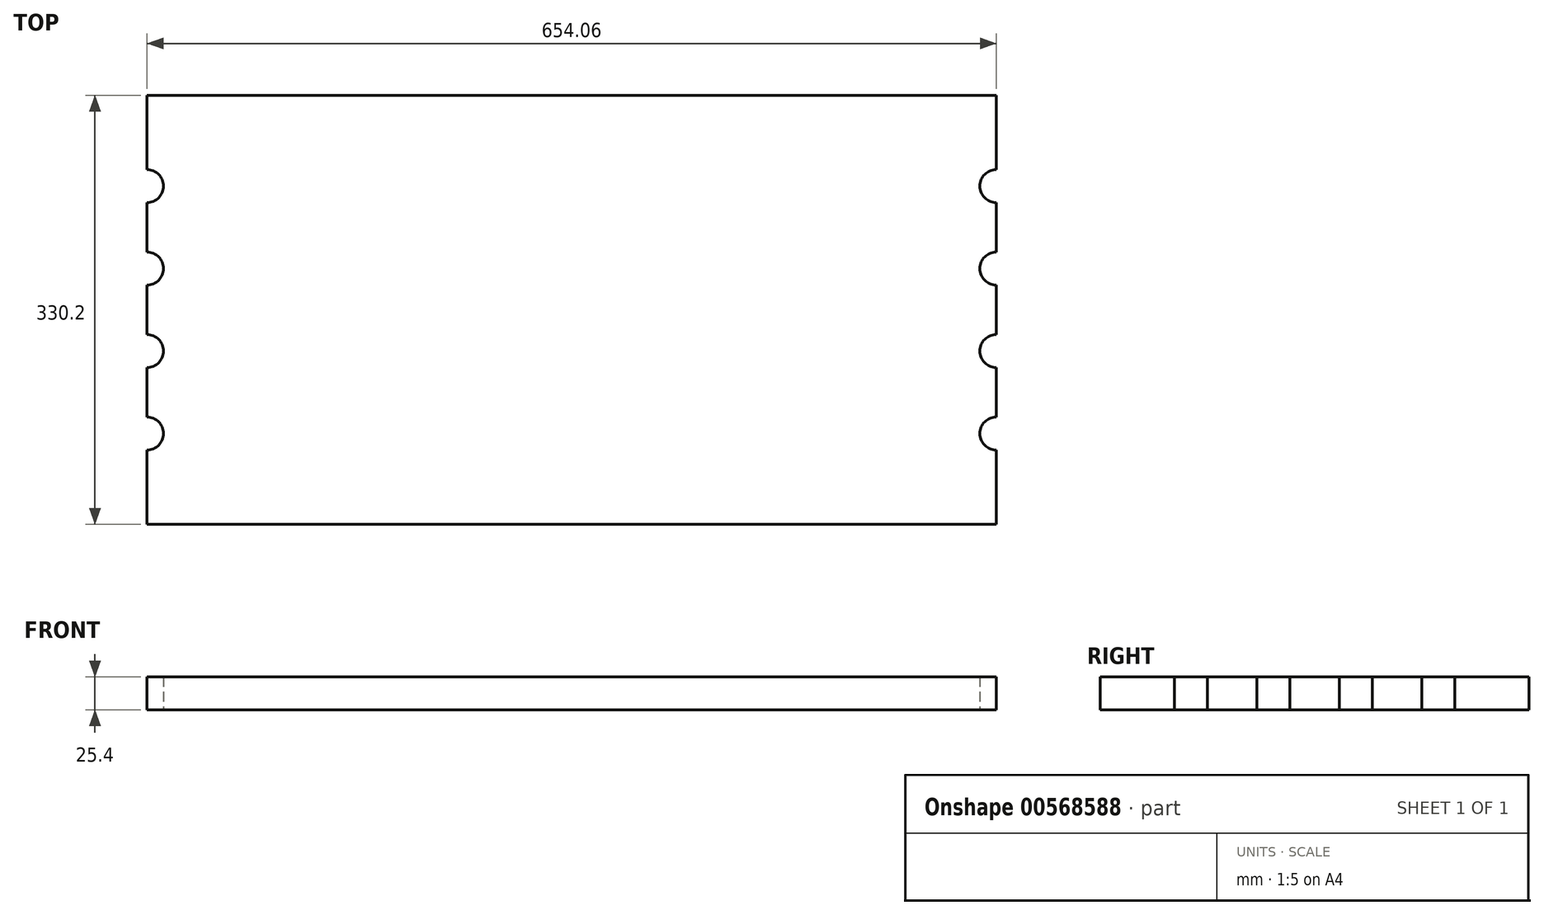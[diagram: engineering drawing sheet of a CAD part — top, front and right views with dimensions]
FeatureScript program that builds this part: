
annotation { "Feature Type Name" : "Feature", "Feature Type Description" : "" }
export const myFeature = defineFeature(function(context is Context, id is Id, definition is map)
    precondition{}
    {
        {
            var Q0;
            Q0=qCreatedBy(makeId("Top.planeOp"),FACE);
            var sketch = newSketch(context, id + "F0", { "sketchPlane" : qUnion([Q0])});
            skLineSegment(sketch, "E0.bottom", {"start": v(327.03, 165.1) * mm, "end": v(-327.02, 165.1) * mm});
            skLineSegment(sketch, "E0.top", {"start": v(327.02, -165.1) * mm, "end": v(-327.03, -165.1) * mm});
            skLineSegment(sketch, "E0.left", {"start": v(327.03, 165.1) * mm, "end": v(327.03, 107.95) * mm});
            skLineSegment(sketch, "E0.right", {"start": v(-327.02, 165.1) * mm, "end": v(-327.02, 107.95) * mm});
            skPoint(sketch, "E0.middle", {"position": v(0, 0) * mm});
            skLineSegment(sketch, "E1", {"start": v(-327.03, -165.1) * mm, "end": v(-327.03, -107.95) * mm});
            skLineSegment(sketch, "E2", {"start": v(-327.02, -82.55) * mm, "end": v(-327.02, -44.45) * mm});
            skLineSegment(sketch, "E3", {"start": v(-327.02, -19.05) * mm, "end": v(-327.02, 19.05) * mm});
            skLineSegment(sketch, "E4", {"start": v(-327.02, 44.45) * mm, "end": v(-327.02, 82.55) * mm});
            skLineSegment(sketch, "E5", {"start": v(-327.02, 107.95) * mm, "end": v(-327.02, 165.1) * mm});
            skArc(sketch, "E6", {"start": v(-327.03, -107.95) * mm, "mid": v(-314.33, -95.25) * mm, "end": v(-327.03, -82.55) * mm});
            skArc(sketch, "E7", {"start": v(-327.02, -44.45) * mm, "mid": v(-314.32, -31.75) * mm, "end": v(-327.02, -19.05) * mm});
            skLineSegment(sketch, "E8.trimOffspring", {"start": v(-327.02, -107.95) * mm, "end": v(-327.02, -165.1) * mm});
            skLineSegment(sketch, "E9.trimOffspring", {"start": v(-327.02, -44.45) * mm, "end": v(-327.02, -82.55) * mm});
            skArc(sketch, "E10", {"start": v(-327.02, 19.05) * mm, "mid": v(-314.32, 31.75) * mm, "end": v(-327.02, 44.45) * mm});
            skArc(sketch, "E11", {"start": v(-327.02, 82.55) * mm, "mid": v(-314.32, 95.25) * mm, "end": v(-327.02, 107.95) * mm});
            skLineSegment(sketch, "E12.trimOffspring", {"start": v(-327.02, 19.05) * mm, "end": v(-327.02, -19.05) * mm});
            skLineSegment(sketch, "E13", {"start": v(0, 165.1) * mm, "end": v(0, -165.1) * mm});
            skArc(sketch, "E14.MirrorCS", {"start": v(327.02, 82.55) * mm, "mid": v(314.33, 95.25) * mm, "end": v(327.03, 107.95) * mm});
            skArc(sketch, "E15.MirrorCS", {"start": v(327.02, 19.05) * mm, "mid": v(314.32, 31.75) * mm, "end": v(327.02, 44.45) * mm});
            skArc(sketch, "E16.MirrorCS", {"start": v(327.02, -44.45) * mm, "mid": v(314.32, -31.75) * mm, "end": v(327.02, -19.05) * mm});
            skArc(sketch, "E17.MirrorCS", {"start": v(327.02, -107.95) * mm, "mid": v(314.32, -95.25) * mm, "end": v(327.02, -82.55) * mm});
            skLineSegment(sketch, "E18.trimOffspring", {"start": v(327.03, 82.55) * mm, "end": v(327.03, 44.45) * mm});
            skLineSegment(sketch, "E19.trimOffspring", {"start": v(327.03, 19.05) * mm, "end": v(327.03, -19.05) * mm});
            skLineSegment(sketch, "E20.trimOffspring", {"start": v(327.03, -44.45) * mm, "end": v(327.03, -82.55) * mm});
            skLineSegment(sketch, "E21.trimOffspring", {"start": v(327.03, -107.95) * mm, "end": v(327.03, -165.1) * mm});
            skSolve(sketch);
        }
        {
            var Q0;
            Q0=makeQuery(id+"F0.imprint","IMPRINT",FACE,{"disambiguationData":[TD([[makeQuery(id+"F0.imprint","IMPRINT",EDGE,{"derivedFrom":sQuery(id+"F0.wireOp",EDGE,"E0.bottom")}),1.0]])]});
            extrude(context, id + "F1", {"entities" : qUnion([Q0]), "depth" : 25.4 * mm, "offsetDistance" : 25.4 * mm});
        }
    });
